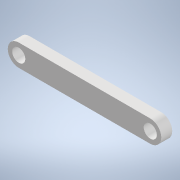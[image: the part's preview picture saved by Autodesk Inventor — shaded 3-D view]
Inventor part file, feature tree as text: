
AUTODESK INVENTOR PART (.ipt)
format: ipt  version: 2022 (Build 260153000, 153)  size: 106,496 bytes
history: native  units: mm
features: extrude x1, sketch x1
ambient origin geometry x8: Origin, YZ Plane, XZ Plane, XY Plane, X Axis, Y Axis, Z Axis, Center Point
bodies: Solid1 (feature_tree)
feature tree (2):
  extrude  "Extrusion1"  Depth=5.0mm
  sketch  "Sketch1"  dims[d0=10.0mm d1=6.0mm d3=60.0mm d4=5.0mm d5=0.0mm]
